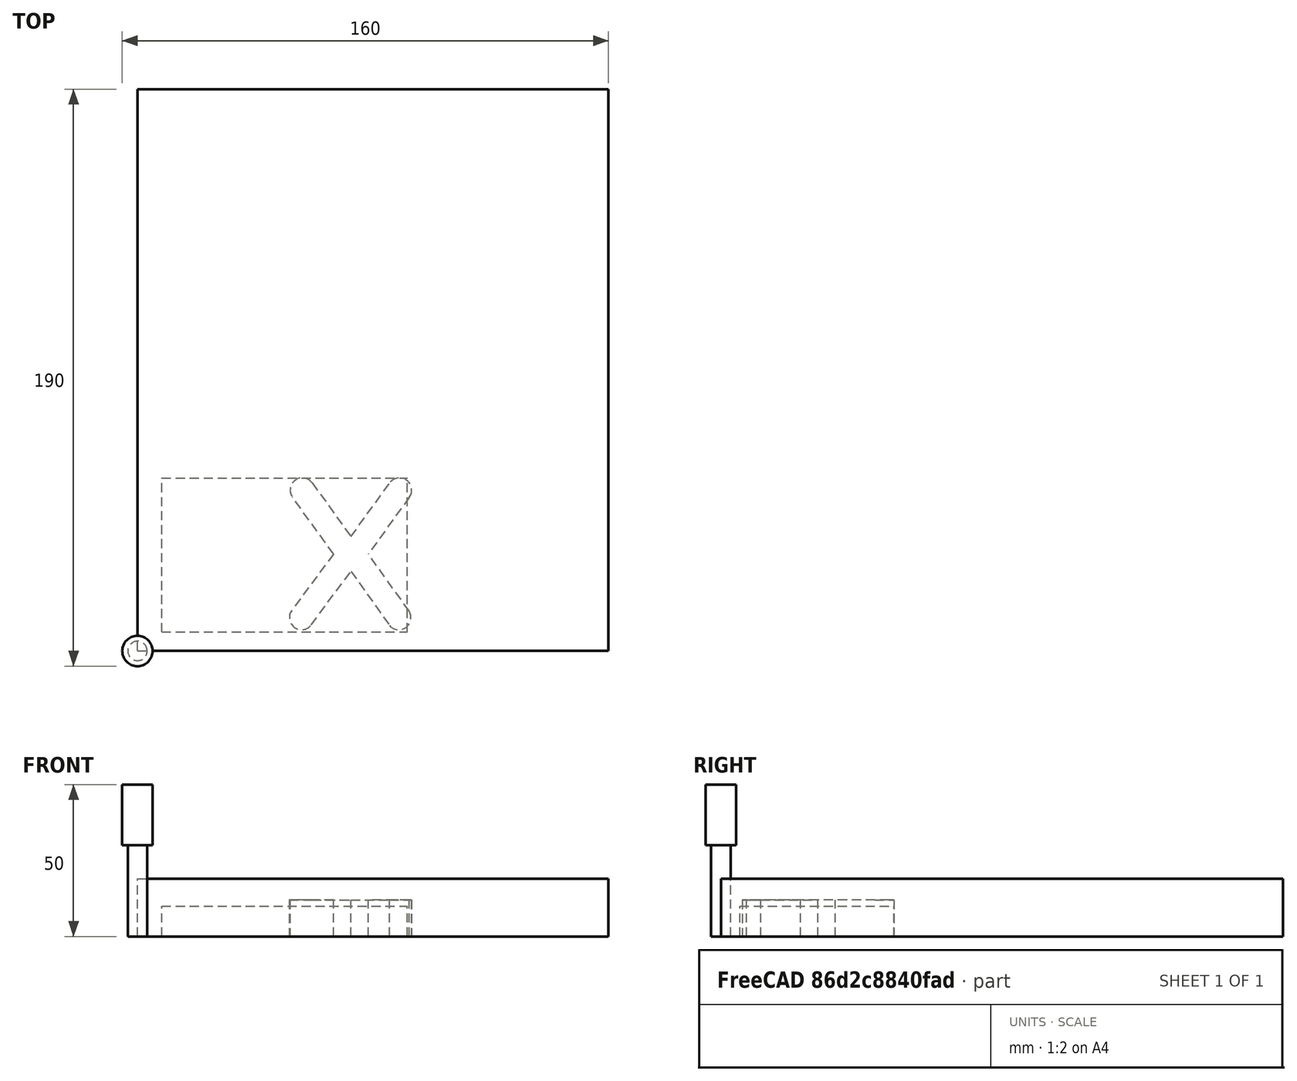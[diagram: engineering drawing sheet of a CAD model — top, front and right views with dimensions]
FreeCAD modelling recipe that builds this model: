
FCSTD DOCUMENT  (FreeCAD 0.21Rpre_29217.fc36 (Git))
Label: JohnXOV2
License: All rights reserved
LicenseURL: http://en.wikipedia.org/wiki/All_rights_reserved
objects: Path::FeaturePython×8, Part::FeaturePython×7, App::DocumentObjectGroup×6, Sketcher::SketchObject×4, PartDesign::Pad×3, PartDesign::Body×3, App::FeaturePython×2, PartDesign::Pocket×1, Mesh::FeaturePython×1
note: 25 computed .brp shape members not serialized (recipe doc carries the construction recipe); baked Part::Feature solids carry a one-line shape summary decoded from their .brp

FEATURE [Sketcher::SketchObject] Sketch
  FullyConstrained = true
  MapMode = 5
  Support = -> [XY_Plane]
  sketch-geometry (8):
    g0: ArcOfCircle CenterX=28 CenterY=37 CenterZ=0 NormalX=0 NormalY=0 NormalZ=1 AngleXU=0 Radius=20 StartAngle=1.44e-14 EndAngle=3.14159
    g1: ArcOfCircle CenterX=28 CenterY=27 CenterZ=0 NormalX=0 NormalY=0 NormalZ=1 AngleXU=0 Radius=20 StartAngle=3.14159 EndAngle=6.28319
    g2: LineSegment StartX=8 StartY=37 StartZ=0 EndX=8 EndY=27 EndZ=0
    g3: LineSegment StartX=48 StartY=27 StartZ=0 EndX=48 EndY=37 EndZ=0
    g4: ArcOfCircle CenterX=28 CenterY=37 CenterZ=0 NormalX=0 NormalY=0 NormalZ=1 AngleXU=0 Radius=13 StartAngle=-6.031e-13 EndAngle=3.14159
    g5: ArcOfCircle CenterX=28 CenterY=27 CenterZ=0 NormalX=0 NormalY=0 NormalZ=1 AngleXU=0 Radius=13 StartAngle=3.14159 EndAngle=6.28319
    g6: LineSegment StartX=15 StartY=37 StartZ=0 EndX=15 EndY=27 EndZ=0
    g7: LineSegment StartX=41 StartY=27 StartZ=0 EndX=41 EndY=37 EndZ=0
  constraints (18):
    c: Tangent(g0,g2) = -1.5708
    c: Tangent(g2,g1) = -1.5708
    c: Tangent(g1,g3) = -1.5708
    c: Tangent(g3,g0) = -1.5708
    c: Equal(g0,g1)
    c: Vertical(g2)
    c: Tangent(g4,g6) = -1.5708
    c: Tangent(g6,g5) = -1.5708
    c: Tangent(g5,g7) = -1.5708
    c: Tangent(g7,g4) = -1.5708
    c: Equal(g4,g5)
    c: Coincident(g4,g0)
    c: DistanceX(g-1,g1) = 8
    c: Coincident(g1,g5)
    c: DistanceX(g5,g1) = 7
    c: Radius(g1) = 20
    c: DistanceY(g-1,g1) = 27
    c: DistanceY(g6,g6) = 10
FEATURE [PartDesign::Pad] Pad
  Direction = (0,0,1)
  Length = 12
  Length2 = 10
  Profile = -> Sketch
  ReferenceAxis = -> Sketch [N_Axis]
  Type = 0
FEATURE [PartDesign::Body] Body  label="Naught"
  Group = -> [Sketch,Pad]
  Origin = -> Origin
  Tip = -> Pad
FEATURE [Sketcher::SketchObject] Sketch001
  FullyConstrained = false
  MapMode = 5
  Support = -> [XY_Plane001]
  sketch-geometry (22):
    g0: LineSegment StartX=64.5202 StartY=31.9394 StartZ=0 EndX=75.9699 EndY=31.9394 EndZ=0
    g1: LineSegment StartX=70.245 StartY=37.6765 StartZ=0 EndX=70.245 EndY=26.2268 EndZ=0
    g2: LineSegment StartX=70.245 StartY=37.6765 StartZ=0 EndX=83.0022 EndY=55.3418 EndZ=0
    g3: ArcOfCircle CenterX=86.245 CenterY=53 CenterZ=0 NormalX=0 NormalY=0 NormalZ=1 AngleXU=0 Radius=4 StartAngle=5.65774 EndAngle=8.79933
    g4: LineSegment StartX=89.4878 StartY=50.6582 StartZ=0 EndX=75.9699 EndY=31.9394 EndZ=0
    g5: LineSegment StartX=64.5202 StartY=31.9394 StartZ=0 EndX=51.0022 EndY=50.6582 EndZ=0
    g6: ArcOfCircle CenterX=54.245 CenterY=53 CenterZ=0 NormalX=0 NormalY=0 NormalZ=1 AngleXU=0 Radius=4 StartAngle=0.625446 EndAngle=3.76703
    g7: LineSegment StartX=57.4878 StartY=55.3418 StartZ=0 EndX=70.245 EndY=37.6765 EndZ=0
    g8: LineSegment StartX=64.5202 StartY=31.9394 StartZ=0 EndX=50.7847 EndY=13.3795 EndZ=0
    g9: ArcOfCircle CenterX=54 CenterY=11 CenterZ=0 NormalX=0 NormalY=0 NormalZ=1 AngleXU=0 Radius=4 StartAngle=2.50448 EndAngle=5.64607
    g10: LineSegment StartX=57.2153 StartY=8.6205 StartZ=0 EndX=70.245 EndY=26.2268 EndZ=0
    g11: LineSegment StartX=70.245 StartY=26.2268 StartZ=0 EndX=82.9645 EndY=8.39507 EndZ=0
    g12: ArcOfCircle CenterX=86 CenterY=11 CenterZ=0 NormalX=0 NormalY=0 NormalZ=1 AngleXU=0 Radius=4 StartAngle=3.8508 EndAngle=6.84824
    g13: LineSegment StartX=89.3782 StartY=13.1419 StartZ=0 EndX=75.9699 EndY=31.9394 EndZ=0
    g14: LineSegment StartX=54.245 StartY=53 StartZ=0 EndX=86.245 EndY=53 EndZ=0
    g15: LineSegment StartX=54 StartY=11 StartZ=0 EndX=86 EndY=11 EndZ=0
    g16: LineSegment StartX=54.245 StartY=53 StartZ=0 EndX=86 EndY=11 EndZ=0
    g17: LineSegment StartX=51.0022 StartY=50.6582 StartZ=0 EndX=57.4878 EndY=55.3418 EndZ=0
    g18: LineSegment StartX=83.0022 StartY=55.3418 StartZ=0 EndX=89.4878 EndY=50.6582 EndZ=0
    g19: LineSegment StartX=50.7847 StartY=13.3795 StartZ=0 EndX=57.2153 EndY=8.6205 EndZ=0
    g20: LineSegment StartX=82.9645 StartY=8.39507 StartZ=0 EndX=89.2913 EndY=17.2884 EndZ=0
    g21: LineSegment StartX=86.245 StartY=53 StartZ=0 EndX=54 EndY=11 EndZ=0
  constraints (59):
    c: Parallel(g5,g7)
    c: Parallel(g2,g4)
    c: Parallel(g8,g10)
    c: Parallel(g11,g13)
    c: Coincident(g14,g6)
    c: Coincident(g14,g3)
    c: Coincident(g15,g9)
    c: Coincident(g15,g12)
    c: Horizontal(g15)
    c: Parallel(g14,g-1)
    c: Equal(g7,g2)
    c: Equal(g5,g4)
    c: Equal(g8,g13)
    c: Equal(g10,g11)
    c: DistanceX(g15,g15) = 32
    c: DistanceX(g14,g14) = 32
    c: Coincident(g16,g6)
    c: Coincident(g16,g12)
    c: Coincident(g6,g5)
    c: Coincident(g7,g6)
    c: Coincident(g2,g3)
    c: Coincident(g4,g3)
    c: Diameter(g6) = 8
    c: Diameter(g3) = 8
    c: Diameter(g12) = 8
    c: Diameter(g9) = 8
    c: Coincident(g11,g12)
    c: Coincident(g12,g13)
    c: Coincident(g13,g0)
    c: Coincident(g8,g0)
    c: Coincident(g5,g8)
    c: Coincident(g9,g8)
    c: Coincident(g9,g10)
    c: Coincident(g10,g11)
    c: Coincident(g1,g10)
    c: Coincident(g13,g4)
    c: Coincident(g1,g7)
    c: Coincident(g2,g7)
    c: Parallel(g0,g-1)
    c: Parallel(g1,g-2)
    c: Equal(g5,g8)
    c: DistanceY(g9,g6) = 42
    c: Coincident(g17,g5)
    c: Coincident(g17,g6)
    c: Perpendicular(g7,g17)
    c: Distance(g17) = 8
    c: Coincident(g18,g2)
    c: Coincident(g18,g3)
    c: Distance(g18) = 8
    c: Coincident(g19,g8)
    c: Coincident(g19,g9)
    c: Distance(g19) = 8
    c: Perpendicular(g8,g19)
    c: Coincident(g20,g11)
    c: Coincident(g21,g3)
    c: Coincident(g21,g9)
    c: DistanceY(g-1,g9) = 11
    c: Equal(g0,g1)
    c: DistanceX(g-1,g9) = 54
FEATURE [PartDesign::Pad] Pad001
  Direction = (0,0,1)
  Length = 12
  Length2 = 10
  Profile = -> Sketch001
  ReferenceAxis = -> Sketch001 [N_Axis]
  Type = 0
FEATURE [PartDesign::Body] Body001  label="Cross"
  Group = -> [Sketch001,Pad001]
  Origin = -> Origin001
  Tip = -> Pad001
FEATURE [App::FeaturePython] SetupSheet  # Path/CAM operation (typed FeaturePython)
  ClearanceHeightExpression = OpStockZMax+SetupSheet.ClearanceHeightOffset
  ClearanceHeightOffset = 5
  CoolantMode = 0
  CoolantModes = None | Flood | Mist
  FinalDepthExpression = OpFinalDepth
  HorizRapid = 0
  SafeHeightExpression = OpStockZMax+SetupSheet.SafeHeightOffset
  SafeHeightOffset = 3
  StartDepthExpression = OpStartDepth
  StepDownExpression = OpToolDiameter
  VertRapid = 0
FEATURE [Part::FeaturePython] Clone  label="Model-Cross"  # Draft clone (typed FeaturePython)
  AttacherType = Attacher::AttachEngine3D
  Fuse = false
  Objects = -> [Body001]
  PathResource = Model
  Scale = (1,1,1)
FEATURE [Part::FeaturePython] Clone001  label="Model-Naught"  # Draft clone (typed FeaturePython)
  AttacherType = Attacher::AttachEngine3D
  Fuse = false
  Objects = -> [Body]
  PathResource = Model
  Scale = (1,1,1)
FEATURE [App::DocumentObjectGroup] Model
  Group = -> [Clone,Clone001]
FEATURE [Part::FeaturePython] Stock001  # WARN: FeaturePython — macro-defined, semantics opaque (R4)
  Height = 10
  Length = 80.73
  Placement = pos=(8,6.25066,0) rot=(0,0,1;0rad)
  StockType = CreateBox
  Width = 50.75
FEATURE [Part::FeaturePython] ToolBit001  label="6.4mm Endmill"  # Path/CAM toolbit (typed FeaturePython)
  BitPropertyNames = Chipload | CuttingEdgeHeight | Diameter | Flutes | Length | Material | ShankDiameter | SpindleDirection
  BitShape = <path>
  Chipload = 0
  CuttingEdgeHeight = 30
  Diameter = 6.4
  File = <userpath>/MensShed/CNCRouter/FreeCAD/Bit/6.4mm_Endmill.fctb
  Flutes = 0
  Length = 50
  Material = 0
  ShankDiameter = 10
  ShapeName = endmill
  SpindleDirection = 0
FEATURE [Path::FeaturePython] __4mm_Endmill  label="6.4mm Endmill001"  # Path/CAM operation (typed FeaturePython)
  HorizFeed = 0.166667
  HorizRapid = 0
  SpindleDir = 0
  SpindleSpeed = 13000
  Tool = -> ToolBit001
  ToolNumber = 2
  VertFeed = 0.0833333
  VertRapid = 0
  expr: HorizRapid = SetupSheet.HorizRapid
  expr: VertRapid = SetupSheet.VertRapid
FEATURE [App::DocumentObjectGroup] Tools
  Group = -> [__4mm_Endmill]
FEATURE [Path::FeaturePython] Profile  # Path/CAM operation (typed FeaturePython)
  Active = true
  AreaParams:
    Tolerance = 1e-07
    FitArcs = True
    Simplify = False
    CleanDistance = 0.0
    Accuracy = 0.01
    Unit = 1.0
    MinArcPoints = 4
    MaxArcPoints = 100
    ClipperScale = 10000000.0
    Fill = 0
    Coplanar = 0
    Reorient = True
    Outline = False
    Explode = False
    OpenMode = 0
    Deflection = 0.01
    SubjectFill = 0
    ClipFill = 0
    Offset = 3.2
    ExtraPass = 0
    Stepover = 0.0
    LastStepover = 0.0
    JoinType = 0
    EndType = 0
    MiterLimit = 2.0
    RoundPrecision = 0.0
    PocketMode = 0
    ToolRadius = 1.0
    PocketExtraOffset = 0.0
    PocketStepover = 0.0
    PocketLastStepover = 0.0
    FromCenter = False
    Angle = 45.0
    AngleShift = 0.0
    Shift = 0.0
    Thicken = False
    SectionCount = -1
    Stepdown = 1.0
    SectionOffset = 0.0
    SectionTolerance = 1e-06
    SectionMode = 2
    Project = False
  ClearanceHeight = 15
  CoolantMode = 0
  CycleTime = 02:35:40
  Direction = 0
  FinalDepth = 0
  HandleMultipleFeatures = 0
  JoinType = 0
  MiterLimit = 0.1
  OffsetExtra = 0
  OpFinalDepth = 0
  OpStartDepth = 10
  OpStockZMax = 10
  OpStockZMin = 0
  OpToolDiameter = 6.4
  PathParams = {'orientation': 1, 'feedrate': 0.1666666666666667, 'feedrate_v': 0.0833333333333333, 'verbose': True, 'resume_height': 13.0, 'retraction': 15.0, 'return_end': True, 'preamble': False, 'start': Vector (44.40419816408473, 53.40323183724682, 15.0)}
  SafeHeight = 13
  Side = 0
  SplitArcs = false
  StartDepth = 11
  StartPoint = (0,0,0)
  StepDown = 3
  ToolController = -> __4mm_Endmill
  UseComp = true
  UseStartPoint = false
  processCircles = false
  processHoles = false
  processPerimeter = true
  expr: ClearanceHeight = OpStockZMax + SetupSheet.ClearanceHeightOffset
  expr: FinalDepth = OpFinalDepth
  expr: SafeHeight = OpStockZMax + SetupSheet.SafeHeightOffset
  expr: StartDepth = 11
  expr: StepDown = 3
FEATURE [Path::FeaturePython] Profile001  # Path/CAM operation (typed FeaturePython)
  Active = true
  AreaParams:
    Tolerance = 1e-07
    FitArcs = True
    Simplify = False
    CleanDistance = 0.0
    Accuracy = 0.01
    Unit = 1.0
    MinArcPoints = 4
    MaxArcPoints = 100
    ClipperScale = 10000000.0
    Fill = 0
    Coplanar = 0
    Reorient = True
    Outline = False
    Explode = False
    OpenMode = 0
    Deflection = 0.01
    SubjectFill = 0
    ClipFill = 0
    Offset = -3.2
    ExtraPass = 0
    Stepover = 0.0
    LastStepover = 0.0
    JoinType = 0
    EndType = 0
    MiterLimit = 2.0
    RoundPrecision = 0.0
    PocketMode = 0
    ToolRadius = 1.0
    PocketExtraOffset = 0.0
    PocketStepover = 0.0
    PocketLastStepover = 0.0
    FromCenter = False
    Angle = 45.0
    AngleShift = 0.0
    Shift = 0.0
    Thicken = False
    SectionCount = -1
    Stepdown = 1.0
    SectionOffset = 0.0
    SectionTolerance = 1e-06
    SectionMode = 2
    Project = False
  Base = -> [Clone001]
  ClearanceHeight = 15
  CoolantMode = 0
  CycleTime = 00:38:52
  Direction = 0
  FinalDepth = 0
  HandleMultipleFeatures = 0
  JoinType = 0
  MiterLimit = 0.1
  OffsetExtra = 0
  OpFinalDepth = 0
  OpStartDepth = 12
  OpStockZMax = 10
  OpStockZMin = 0
  OpToolDiameter = 6.4
  PathParams = {'orientation': 1, 'feedrate': 0.1666666666666667, 'feedrate_v': 0.0833333333333333, 'verbose': True, 'resume_height': 13.0, 'retraction': 15.0, 'return_end': True, 'preamble': False}
  SafeHeight = 13
  Side = 1
  SplitArcs = false
  StartDepth = 11
  StartPoint = (0,0,0)
  StepDown = 3
  ToolController = -> __4mm_Endmill
  UseComp = true
  UseStartPoint = false
  processCircles = false
  processHoles = false
  processPerimeter = true
  expr: ClearanceHeight = OpStockZMax + SetupSheet.ClearanceHeightOffset
  expr: FinalDepth = OpFinalDepth
  expr: SafeHeight = OpStockZMax + SetupSheet.SafeHeightOffset
  expr: StartDepth = 11
  expr: StepDown = 3
FEATURE [App::DocumentObjectGroup] Operations
  Group = -> [Profile,Profile001]
FEATURE [Sketcher::SketchObject] Sketch002
  FullyConstrained = true
  MapMode = 5
  Support = -> [XY_Plane002]
  sketch-geometry (4):
    g0: LineSegment StartX=0 StartY=184 StartZ=0 EndX=155 EndY=184 EndZ=0
    g1: LineSegment StartX=155 StartY=184 StartZ=0 EndX=155 EndY=0 EndZ=0
    g2: LineSegment StartX=155 StartY=0 StartZ=0 EndX=0 EndY=0 EndZ=0
    g3: LineSegment StartX=0 StartY=0 StartZ=0 EndX=0 EndY=184 EndZ=0
  constraints (11):
    c: Coincident(g0,g1)
    c: Coincident(g1,g2)
    c: Coincident(g2,g3)
    c: Coincident(g3,g0)
    c: Horizontal(g0)
    c: Horizontal(g2)
    c: Vertical(g1)
    c: Vertical(g3)
    c: Coincident(g2,g-1)
    c: DistanceY(g3,g3) = 184
    c: DistanceX(g2,g2) = 155
FEATURE [PartDesign::Pad] Pad002
  Direction = (0,0,1)
  Length = 19
  Length2 = 10
  Profile = -> Sketch002
  ReferenceAxis = -> Sketch002 [N_Axis]
  Type = 0
FEATURE [Sketcher::SketchObject] Sketch003
  FullyConstrained = true
  MapMode = 5
  Placement = pos=(0,0,19) rot=(0,0,1;0rad)
  Support = -> [Pad002]
  sketch-geometry (8):
    g0: LineSegment StartX=9 StartY=13.5 StartZ=0 EndX=9 EndY=56 EndZ=0
    g1: ArcOfCircle CenterX=13.5 CenterY=56 CenterZ=0 NormalX=0 NormalY=0 NormalZ=1 AngleXU=0 Radius=4.5 StartAngle=1.5708 EndAngle=3.14159
    g2: LineSegment StartX=13.5 StartY=60.5 StartZ=0 EndX=46 EndY=60.5 EndZ=0
    g3: ArcOfCircle CenterX=46 CenterY=56 CenterZ=0 NormalX=0 NormalY=0 NormalZ=1 AngleXU=0 Radius=4.5 StartAngle=6e-16 EndAngle=1.5708
    g4: LineSegment StartX=50.5 StartY=56 StartZ=0 EndX=50.5 EndY=13.5 EndZ=0
    g5: ArcOfCircle CenterX=46 CenterY=13.5 CenterZ=0 NormalX=0 NormalY=0 NormalZ=1 AngleXU=0 Radius=4.5 StartAngle=4.71239 EndAngle=6.28319
    g6: LineSegment StartX=46 StartY=9 StartZ=0 EndX=13.5 EndY=9 EndZ=0
    g7: ArcOfCircle CenterX=13.5 CenterY=13.5 CenterZ=0 NormalX=0 NormalY=0 NormalZ=1 AngleXU=0 Radius=4.5 StartAngle=3.14159 EndAngle=4.71239
  constraints (21):
    c: Vertical(g0)
    c: Tangent(g0,g1) = 1.5708
    c: Tangent(g1,g2) = 1.5708
    c: Tangent(g2,g3) = 1.5708
    c: Tangent(g3,g4) = 1.5708
    c: Tangent(g4,g5) = 1.5708
    c: Tangent(g5,g6) = 1.5708
    c: Tangent(g6,g7) = 1.5708
    c: Coincident(g7,g0)
    c: Equal(g0,g4)
    c: Equal(g2,g6)
    c: Perpendicular(g6,g0)
    c: Perpendicular(g4,g2)
    c: Radius(g1) = 4.5
    c: Radius(g7) = 4.5
    c: Radius(g5) = 4.5
    c: Radius(g3) = 4.5
    c: DistanceY(g6,g1) = 51.5
    c: DistanceX(g0,g4) = 41.5
    c: DistanceY(g-1,g6) = 9
    c: DistanceX(g-1,g0) = 9
FEATURE [PartDesign::Pocket] Pocket
  BaseFeature = -> Pad002
  Direction = (0,0,-1)
  Length = 6
  Length2 = 5
  Profile = -> Sketch003
  ReferenceAxis = -> Sketch003 [N_Axis]
  Type = 0
FEATURE [PartDesign::Body] Body002  label="Board"
  Group = -> [Sketch002,Pad002,Sketch003,Pocket]
  Origin = -> Origin002
  Tip = -> Pocket
FEATURE [Path::FeaturePython] Job  label="LettersJob"  # Path/CAM operation (typed FeaturePython)
  CycleTime = 03:14:32
  Fixtures = G54
  GeometryTolerance = 0.01
  Group = -> [Body002]
  JobType = 0
  Model = -> Model
  Operations = -> Operations
  OrderOutputBy = 0
  PostProcessor = 11
  PostProcessorOutputFile = %D/%XO.ngc
  SetupSheet = -> SetupSheet
  SplitOutput = false
  Stock = -> Stock001
  Tools = -> Tools
FEATURE [App::FeaturePython] SetupSheet001  # Path/CAM operation (typed FeaturePython)
  ClearanceHeightExpression = OpStockZMax+SetupSheet001.ClearanceHeightOffset
  ClearanceHeightOffset = 5
  CoolantMode = 0
  CoolantModes = None | Flood | Mist
  FinalDepthExpression = OpFinalDepth
  HorizRapid = 0
  SafeHeightExpression = OpStockZMax+SetupSheet001.SafeHeightOffset
  SafeHeightOffset = 3
  StartDepthExpression = OpStartDepth
  StepDownExpression = OpToolDiameter
  VertRapid = 0
FEATURE [Part::FeaturePython] Clone002  label="Model-Board"  # Draft clone (typed FeaturePython)
  AttacherType = Attacher::AttachEngine3D
  Fuse = false
  Objects = -> [Body002]
  PathResource = Model
  Scale = (1,1,1)
FEATURE [App::DocumentObjectGroup] Model001
  Group = -> [Clone002]
FEATURE [Part::FeaturePython] Stock002  # WARN: FeaturePython — macro-defined, semantics opaque (R4)
  Height = 19
  Length = 155
  StockType = CreateBox
  Width = 185
FEATURE [Part::FeaturePython] ToolBit002  label="6.4mm Endmill002"  # Path/CAM toolbit (typed FeaturePython)
  BitPropertyNames = Chipload | CuttingEdgeHeight | Diameter | Flutes | Length | Material | ShankDiameter | SpindleDirection
  BitShape = <path>
  Chipload = 0
  CuttingEdgeHeight = 30
  Diameter = 6.4
  File = <userpath>/MensShed/CNCRouter/FreeCAD/Bit/6.4mm_Endmill.fctb
  Flutes = 0
  Length = 50
  Material = 0
  ShankDiameter = 10
  ShapeName = endmill
  SpindleDirection = 0
FEATURE [Path::FeaturePython] __4mm_Endmill002  label="6.4mm Endmill003"  # Path/CAM operation (typed FeaturePython)
  HorizFeed = 15
  HorizRapid = 0
  SpindleDir = 0
  SpindleSpeed = 13000
  Tool = -> ToolBit002
  ToolNumber = 2
  VertFeed = 5
  VertRapid = 0
  expr: HorizRapid = SetupSheet001.HorizRapid
  expr: VertRapid = SetupSheet001.VertRapid
FEATURE [App::DocumentObjectGroup] Tools001
  Group = -> [__4mm_Endmill002]
FEATURE [Path::FeaturePython] Pocket_Shape  # Path/CAM operation (typed FeaturePython)
  Active = true
  AreaParams:
    Tolerance = 1e-07
    FitArcs = True
    Simplify = False
    CleanDistance = 0.0
    Accuracy = 0.01
    Unit = 1.0
    MinArcPoints = 4
    MaxArcPoints = 100
    ClipperScale = 10000000.0
    Fill = 0
    Coplanar = 0
    Reorient = True
    Outline = False
    Explode = False
    OpenMode = 0
    Deflection = 0.01
    SubjectFill = 0
    ClipFill = 0
    Offset = 0.0
    ExtraPass = 0
    Stepover = 0.0
    LastStepover = 0.0
    JoinType = 0
    EndType = 0
    MiterLimit = 2.0
    RoundPrecision = 0.0
    PocketMode = 2
    ToolRadius = 3.2
    PocketExtraOffset = 0.0
    PocketStepover = 3.84
    PocketLastStepover = 0.0
    FromCenter = True
    Angle = 45.0
    AngleShift = 0.0
    Shift = 0.0
    Thicken = False
    SectionCount = -1
    Stepdown = 1.0
    SectionOffset = 0.0
    SectionTolerance = 1e-06
    SectionMode = 2
    Project = False
  Base = -> [Clone002]
  ClearanceHeight = 24
  CoolantMode = 0
  CutMode = 0
  CycleTime = 00:02:03
  ExtensionCorners = true
  ExtensionLengthDefault = 3.2
  ExtraOffset = 0
  FinalDepth = 13
  FinishDepth = 0
  KeepToolDown = false
  MinTravel = false
  OffsetPattern = 1
  OpFinalDepth = 13
  OpStartDepth = 19
  OpStockZMax = 19
  OpStockZMin = 0
  OpToolDiameter = 6.4
  PathParams = {'orientation': 1, 'feedrate': 15.0, 'feedrate_v': 5.0, 'verbose': True, 'resume_height': 22.0, 'retraction': 24.0, 'return_end': True, 'preamble': False}
  PocketLastStepOver = 0
  SafeHeight = 22
  SplitArcs = false
  StartAt = 0
  StartDepth = 19
  StartPoint = (0,0,0)
  StepDown = 3
  StepOver = 60
  ToolController = -> __4mm_Endmill002
  UseOutline = false
  UseStartPoint = false
  ZigZagAngle = 45
  expr: ClearanceHeight = OpStockZMax + SetupSheet001.ClearanceHeightOffset
  expr: ExtensionLengthDefault = OpToolDiameter / 2
  expr: FinalDepth = OpFinalDepth
  expr: SafeHeight = OpStockZMax + SetupSheet001.SafeHeightOffset
  expr: StartDepth = OpStartDepth
  expr: StepDown = 3
FEATURE [Path::FeaturePython] Array  # Path/CAM operation (typed FeaturePython)
  Active = true
  Angle = 0
  Base = -> [Pocket_Shape]
  Centre = (0,0,0)
  Copies = 0
  CopiesX = 2
  CopiesY = 2
  JitterMagnitude = (0,0,0)
  JitterPercent = 0
  JitterSeed = 0
  Offset = (47.5,57.5,0)
  SwapDirection = false
  ToolController = -> __4mm_Endmill002
  Type = 1
FEATURE [App::DocumentObjectGroup] Operations001
  Group = -> [Pocket_Shape,Array]
FEATURE [Path::FeaturePython] Job001  label="BoardJob"  # Path/CAM operation (typed FeaturePython)
  CycleTime = 00:02:03
  Fixtures = G54
  GeometryTolerance = 0.01
  JobType = 0
  Model = -> Model001
  Operations = -> Operations001
  OrderOutputBy = 0
  PostProcessor = 11
  PostProcessorOutputFile = %D/%dBoard.ngc
  SetupSheet = -> SetupSheet001
  SplitOutput = false
  Stock = -> Stock002
  Tools = -> Tools001
FEATURE [Mesh::FeaturePython] CutMaterial  # WARN: FeaturePython — macro-defined, semantics opaque (R4)
note: 2 file-system paths scrubbed to <path> (originals preserved in the JSON sidecar)
